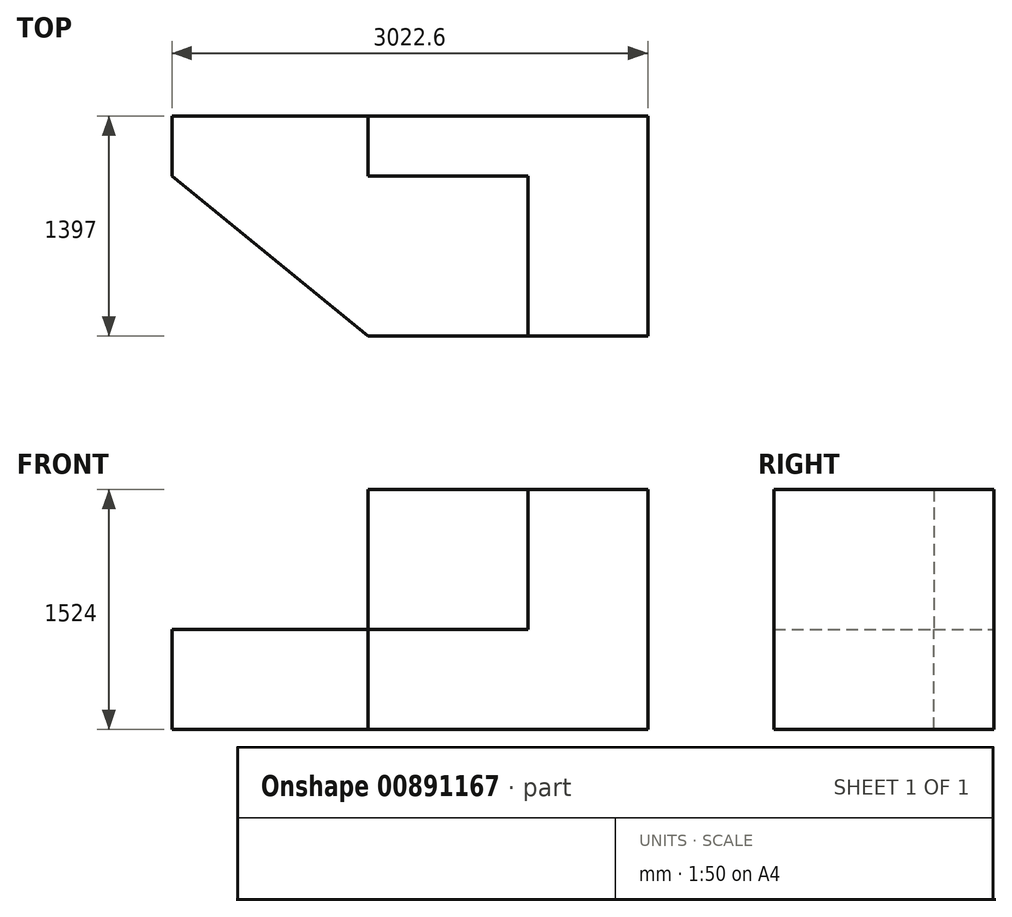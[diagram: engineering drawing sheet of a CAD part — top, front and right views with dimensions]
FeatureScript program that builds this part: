
annotation { "Feature Type Name" : "Feature", "Feature Type Description" : "" }
export const myFeature = defineFeature(function(context is Context, id is Id, definition is map)
    precondition{}
    {
        {
            var Q0;
            Q0=qCreatedBy(makeId("Top.planeOp"),FACE);
            var sketch = newSketch(context, id + "F0", { "sketchPlane" : qUnion([Q0])});
            skLineSegment(sketch, "E0.bottom", {"start": v(0, 0) * mm, "end": v(-3022.6, 0) * mm});
            skLineSegment(sketch, "E0.top", {"start": v(0, 1397) * mm, "end": v(-3022.6, 1397) * mm});
            skLineSegment(sketch, "E0.left", {"start": v(0, 0) * mm, "end": v(0, 1397) * mm});
            skLineSegment(sketch, "E0.right", {"start": v(-3022.6, 0) * mm, "end": v(-3022.6, 1397) * mm});
            skSolve(sketch);
        }
        {
            var Q0;
            Q0=qSketchRegion(id+"F0",true);
            extrude(context, id + "F1", {"entities" : qUnion([Q0]), "depth" : 635 * mm, "offsetDistance" : 25.4 * mm});
        }
        {
            var Q0;
            Q0=makeQuery(id+"F1.opExtrude","CAP_FACE",FACE,{"disambiguationData":[OSD([sQuery(id+"F0.wireOp",EDGE,"E0.bottom"),sQuery(id+"F0.wireOp",EDGE,"E0.top"),sQuery(id+"F0.wireOp",EDGE,"E0.left"),sQuery(id+"F0.wireOp",EDGE,"E0.right")])],"isStart":false});
            var sketch = newSketch(context, id + "F2", { "sketchPlane" : qUnion([Q0])});
            skLineSegment(sketch, "E1", {"start": v(0, 0) * mm, "end": v(-1778, 0) * mm});
            skLineSegment(sketch, "E2", {"start": v(-3022.6, 1397) * mm, "end": v(-3022.6, 1016) * mm});
            skLineSegment(sketch, "E3", {"start": v(-3022.6, 1016) * mm, "end": v(-1778, 0) * mm});
            skSolve(sketch);
        }
        {
            var Q0;
            Q0=qSketchRegion(id+"F2",true);
            var Q1;
            {var subQ0=sQuery(id+"F2.wireOp",EDGE,"E3");Q1=makeQuery(id+"F2.imprint","IMPRINT",FACE,{"disambiguationData":[TD([[makeQuery(id+"F2.imprint","IMPRINT",EDGE,{"derivedFrom":subQ0}),-1.0]])]});}
            extrude(context, id + "F3", {"entities" : qUnion([Q0, Q1]), "operationType" : NewBodyOperationType.REMOVE, "oppositeDirection" : true, "depth" : 815.34 * mm, "offsetDistance" : 25.4 * mm});
        }
        {
            var Q0;
            Q0=makeQuery(id+"F1.opExtrude","CAP_FACE",FACE,{"disambiguationData":[OSD([sQuery(id+"F0.wireOp",EDGE,"E0.bottom"),sQuery(id+"F0.wireOp",EDGE,"E0.top"),sQuery(id+"F0.wireOp",EDGE,"E0.left"),sQuery(id+"F0.wireOp",EDGE,"E0.right")])],"isStart":false});
            var sketch = newSketch(context, id + "F4", { "sketchPlane" : qUnion([Q0])});
            skLineSegment(sketch, "E4", {"start": v(0, 0) * mm, "end": v(-762, 0) * mm});
            skLineSegment(sketch, "E5", {"start": v(-762, 0) * mm, "end": v(-762, 1016) * mm});
            skLineSegment(sketch, "E6", {"start": v(-762, 1016) * mm, "end": v(-1778, 1016) * mm});
            skLineSegment(sketch, "E7", {"start": v(-1778, 1016) * mm, "end": v(-1778, 1397) * mm});
            skLineSegment(sketch, "E8", {"start": v(-1778, 1397) * mm, "end": v(0, 1397) * mm});
            skLineSegment(sketch, "E9", {"start": v(0, 1397) * mm, "end": v(0, 0) * mm});
            skSolve(sketch);
        }
        {
            var Q0;
            Q0=makeQuery(id+"F4.imprint","IMPRINT",FACE,{"disambiguationData":[TD([[makeQuery(id+"F4.imprint","IMPRINT",EDGE,{"derivedFrom":sQuery(id+"F4.wireOp",EDGE,"E4")}),-1.0]])]});
            extrude(context, id + "F5", {"entities" : qUnion([Q0]), "operationType" : NewBodyOperationType.ADD, "depth" : 889 * mm, "offsetDistance" : 25.4 * mm});
        }
    });
